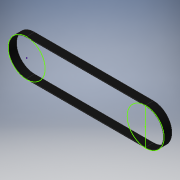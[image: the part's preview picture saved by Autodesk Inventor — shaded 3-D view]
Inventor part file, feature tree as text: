
AUTODESK INVENTOR PART (.ipt)
format: ipt  version: 2016 (Build 200138000, 138)  size: 110,592 bytes
history: native  units: in
note: dims shown in document units (in); Inventor stores cm internally (conversion verified against a paired STEP export)
features: sketch x1, other x1
ambient origin geometry x8: Origin, YZ Plane, XZ Plane, XY Plane, X Axis, Y Axis, Z Axis, Center Point
bodies: Solid1 (feature_tree)
feature tree (2):
  sketch  "Sketch1"
  other  "Boss-Extrude1"
